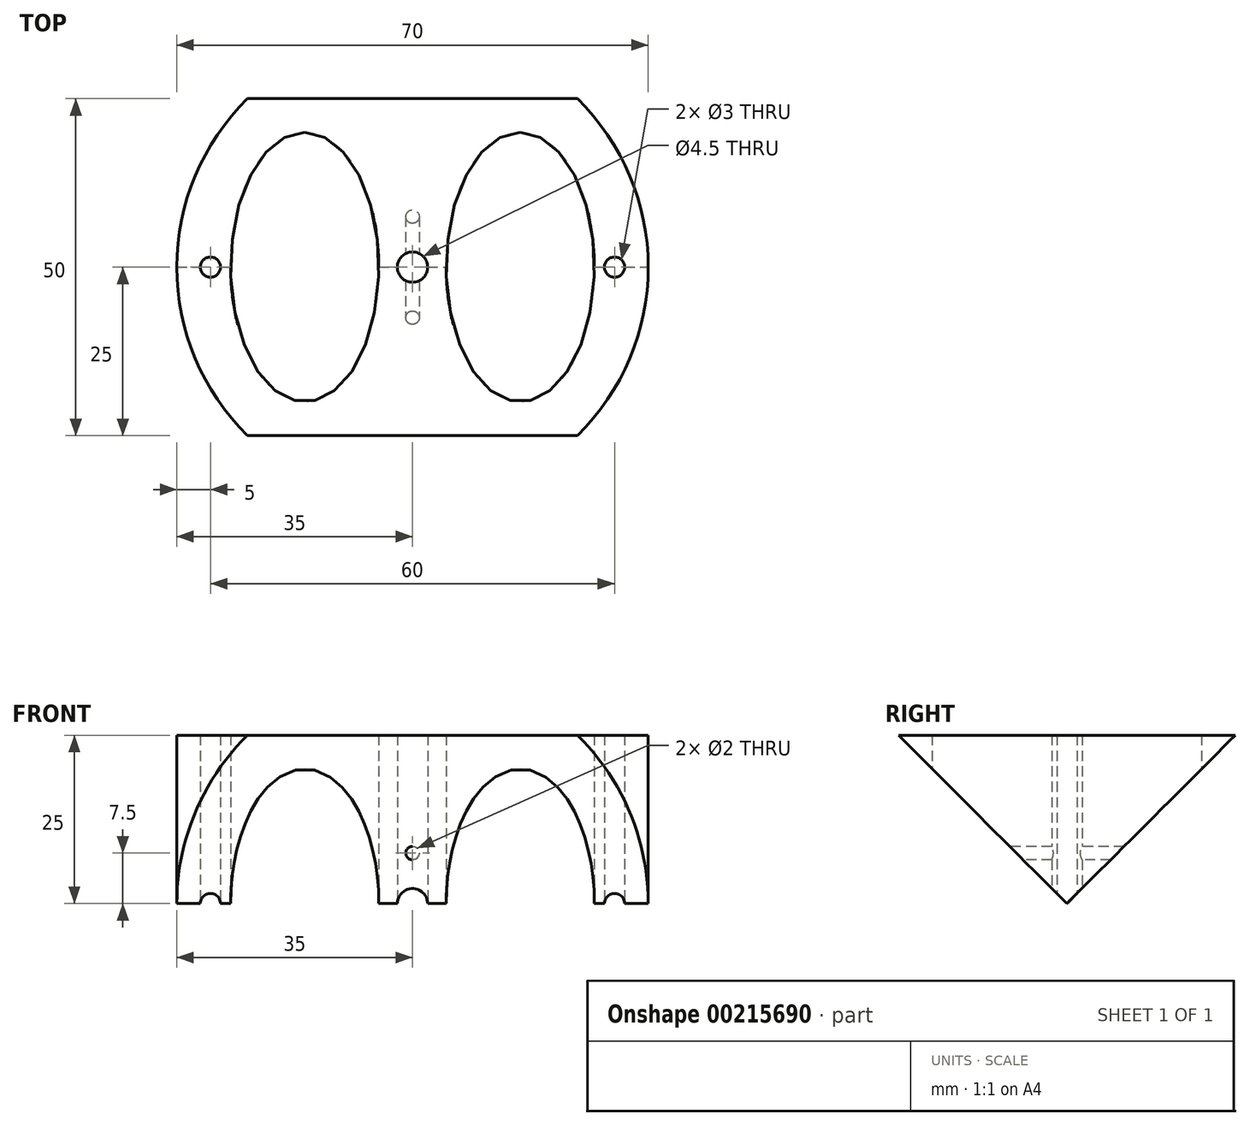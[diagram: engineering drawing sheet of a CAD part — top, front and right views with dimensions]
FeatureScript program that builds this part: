
annotation { "Feature Type Name" : "Feature", "Feature Type Description" : "" }
export const myFeature = defineFeature(function(context is Context, id is Id, definition is map)
    precondition{}
    {
        {
            var Q0;
            Q0=qCreatedBy(makeId("Top.planeOp"),FACE);
            var sketch = newSketch(context, id + "F0", { "sketchPlane" : qUnion([Q0])});
            skCircle(sketch, "E0", {"center": v(0, 0) * mm, "radius": 35 * mm});
            skCircle(sketch, "E1", {"center": v(-30, 0) * mm, "radius": 1.5 * mm});
            skCircle(sketch, "E2.MirrorC", {"center": v(30, 0) * mm, "radius": 1.5 * mm});
            skCircle(sketch, "E3", {"center": v(0, 0) * mm, "radius": 2.25 * mm});
            skEllipse(sketch, "E4", {"center": v(-16, 0) * mm, "majorRadius": 20 * mm, "minorRadius": 11 * mm, "majorAxis": v(0, 1)});
            skEllipse(sketch, "E5.MirrorC", {"center": v(16, 0) * mm, "majorRadius": 20 * mm, "minorRadius": 11 * mm, "majorAxis": v(0, 1)});
            skSolve(sketch);
        }
        {
            var Q0;
            Q0 = qSketchRegion(id + "F0", true);
            extrude(context, id + "F1", {"entities" : qUnion([Q0]), "depth" : 25 * mm});
        }
        {
            var Q0;
            Q0=qCreatedBy(makeId("Right.planeOp"),FACE);
            var sketch = newSketch(context, id + "F2", { "sketchPlane" : qUnion([Q0])});
            skLineSegment(sketch, "E6", {"start": v(0, 0) * mm, "end": v(50, 50) * mm});
            skLineSegment(sketch, "E7", {"start": v(50, 50) * mm, "end": v(50, 0) * mm});
            skLineSegment(sketch, "E8", {"start": v(50, 0) * mm, "end": v(0, 0) * mm});
            skLineSegment(sketch, "E9", {"start": v(0, 0) * mm, "end": v(-50, 0) * mm});
            skLineSegment(sketch, "E10", {"start": v(-50, 0) * mm, "end": v(-50, 50) * mm});
            skLineSegment(sketch, "E11", {"start": v(-50, 50) * mm, "end": v(0, 0) * mm});
            skSolve(sketch);
        }
        {
            var Q0;
            Q0 = qSketchRegion(id + "F2", true);
            extrude(context, id + "F3", {"entities" : qUnion([Q0]), "operationType" : NewBodyOperationType.REMOVE, "endBound" : BoundingType.THROUGH_ALL, "oppositeDirection" : true, "depth" : 25 * mm, "hasSecondDirection" : true, "secondDirectionBound" : SecondDirectionBoundingType.THROUGH_ALL, "secondDirectionOppositeDirection" : false, "secondDirectionDepth" : 25 * mm});
        }
        {
            var Q0;
            Q0=qCreatedBy(makeId("Front.planeOp"),FACE);
            var sketch = newSketch(context, id + "F4", { "sketchPlane" : qUnion([Q0])});
            skCircle(sketch, "E12", {"center": v(0, 7.5) * mm, "radius": 1 * mm});
            skSolve(sketch);
        }
        {
            var Q0;
            Q0 = qSketchRegion(id + "F4", true);
            extrude(context, id + "F5", {"entities" : qUnion([Q0]), "operationType" : NewBodyOperationType.REMOVE, "endBound" : BoundingType.THROUGH_ALL, "oppositeDirection" : true, "depth" : 25 * mm, "hasSecondDirection" : true, "secondDirectionBound" : SecondDirectionBoundingType.THROUGH_ALL, "secondDirectionOppositeDirection" : false, "secondDirectionDepth" : 25 * mm});
        }
    });
